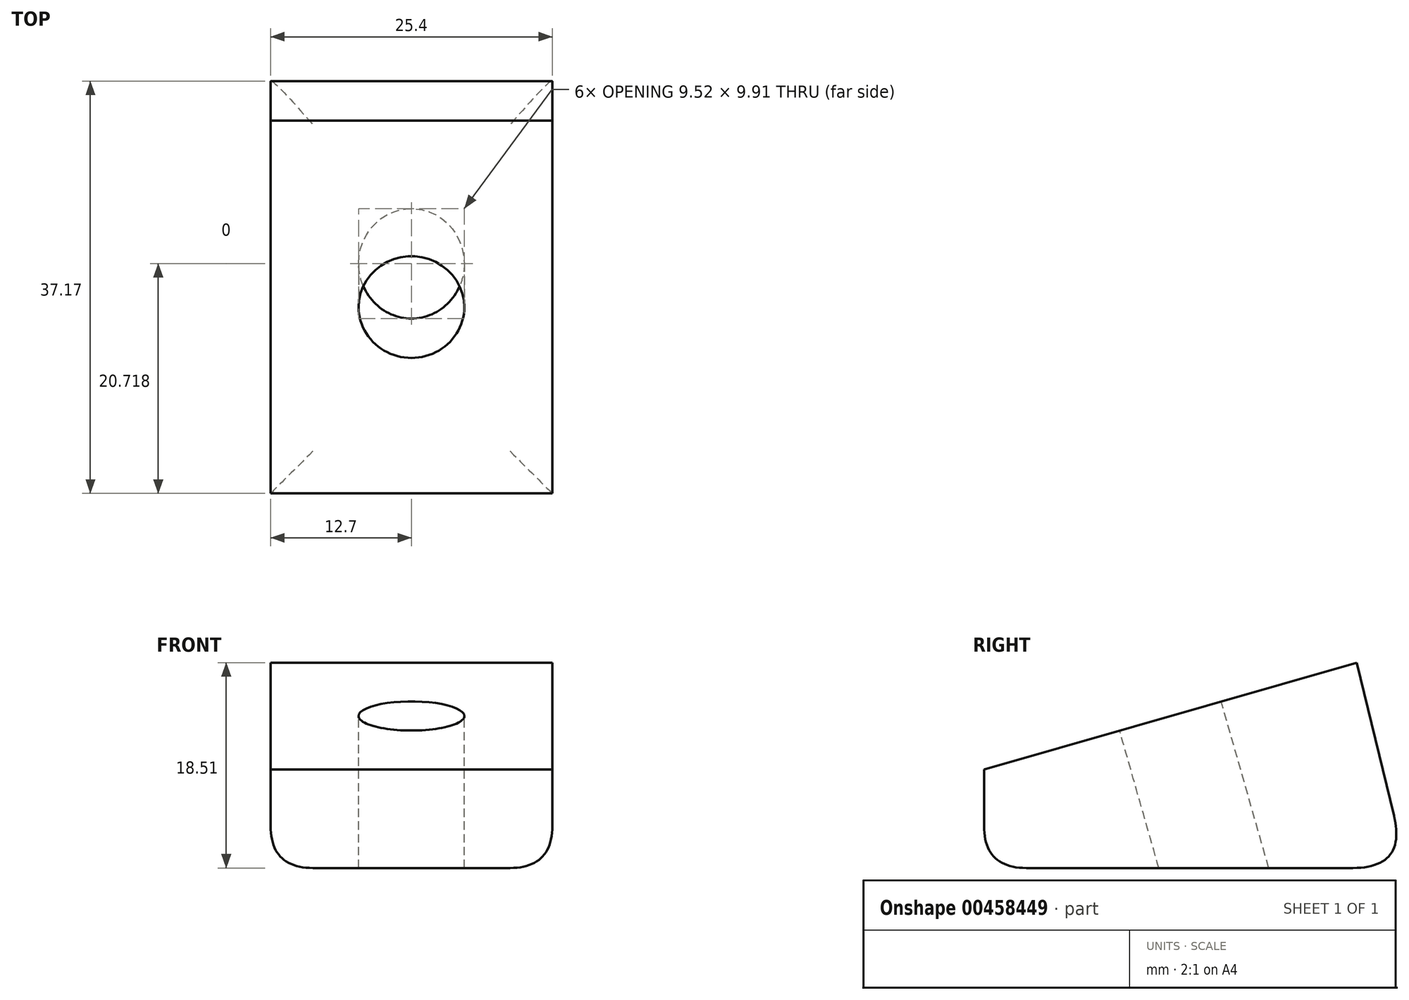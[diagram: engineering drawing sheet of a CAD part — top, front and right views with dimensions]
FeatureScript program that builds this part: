
annotation { "Feature Type Name" : "Feature", "Feature Type Description" : "" }
export const myFeature = defineFeature(function(context is Context, id is Id, definition is map)
    precondition{}
    {
        {
            var Q0;
            Q0=qCreatedBy(makeId("Right.planeOp"),FACE);
            var sketch = newSketch(context, id + "F0", { "sketchPlane" : qUnion([Q0])});
            skLineSegment(sketch, "E0", {"start": v(23.74, 18.51) * mm, "end": v(28.25, 0) * mm});
            skLineSegment(sketch, "E1", {"start": v(28.25, 0) * mm, "end": v(-9.85, 0) * mm});
            skLineSegment(sketch, "E2", {"start": v(-9.85, 0) * mm, "end": v(-9.85, 8.89) * mm});
            skLineSegment(sketch, "E3", {"start": v(-9.85, 8.89) * mm, "end": v(23.74, 18.51) * mm});
            skSolve(sketch);
        }
        {
            var Q0;
            Q0 = qSketchRegion(id + "F0", true);
            extrude(context, id + "F1", {"entities" : qUnion([Q0]), "depth" : 25.4 * mm});
        }
        {
            var Q0;
            Q0=makeQuery(id+"F1.opExtrude","SWEPT_FACE",FACE,{"disambiguationData":[OSD([sQuery(id+"F0.wireOp",EDGE,"E3")])]});
            var sketch = newSketch(context, id + "F2", { "sketchPlane" : qUnion([Q0])});
            skCircle(sketch, "E4", {"center": v(12.7, 10.45) * mm, "radius": 3.18 * mm});
            skSolve(sketch);
        }
        {
            var Q0;
            Q0=makeQuery(id+"F1.opExtrude","SWEPT_EDGE",EDGE,{"disambiguationData":[OSD([sQuery(id+"F0.wireOp",EDGE,"E0"),sQuery(id+"F0.wireOp",EDGE,"E1")])]});
            var Q1;
            Q1=makeQuery(id+"F1.opExtrude","CAP_EDGE",EDGE,{"disambiguationData":[OSD([sQuery(id+"F0.wireOp",EDGE,"E1")])],"isStart":true});
            var Q2;
            Q2=makeQuery(id+"F1.opExtrude","SWEPT_EDGE",EDGE,{"disambiguationData":[OSD([sQuery(id+"F0.wireOp",EDGE,"E1"),sQuery(id+"F0.wireOp",EDGE,"E2")])]});
            var Q3;
            Q3=makeQuery(id+"F1.opExtrude","CAP_EDGE",EDGE,{"disambiguationData":[OSD([sQuery(id+"F0.wireOp",EDGE,"E1")])],"isStart":false});
            fillet(context, id + "F3", {"entities" : qUnion([Q0, Q1, Q2, Q3]), "radius" : 3.8 * mm, "tangentPropagation" : true, "rho" : 0.5, "crossSection" : FilletCrossSection.CONIC, "allowEdgeOverflow" : false});
        }
        {
            var Q0;
            Q0=sQuery(id+"F2.wireOp",VERTEX,"E4.center");
            var Q1;
            Q1=makeQuery(id+"F1.opExtrude","SWEPT_BODY",BODY,{"disambiguationData":[OSD([sQuery(id+"F0.wireOp",EDGE,"E0"),sQuery(id+"F0.wireOp",EDGE,"E1"),sQuery(id+"F0.wireOp",EDGE,"E2"),sQuery(id+"F0.wireOp",EDGE,"E3")])]});
            hole(context, id + "F4", {"style" : HoleStyle.SIMPLE, "endStyle" : HoleEndStyle.THROUGH, "holeDiameter" : 9.52 * mm, "isTappedThrough" : true, "tappedDepth" : 12.7 * mm, "tapClearance" : 3, "locations" : qUnion([Q0]), "scope" : qUnion([Q1])});
        }
    });
